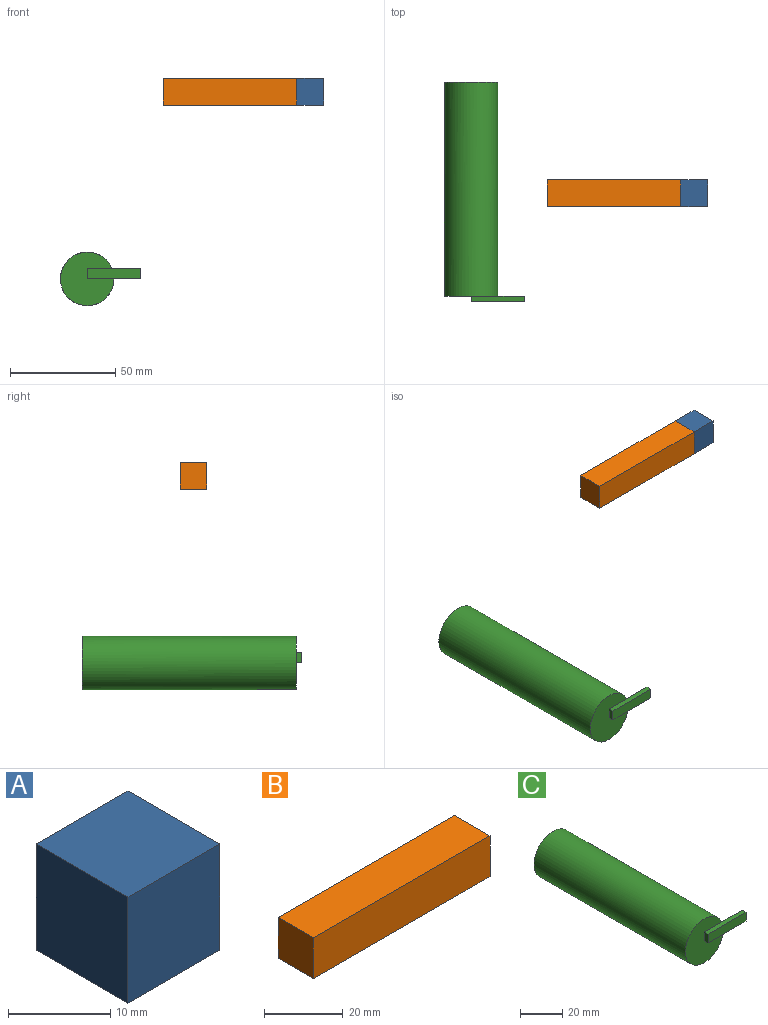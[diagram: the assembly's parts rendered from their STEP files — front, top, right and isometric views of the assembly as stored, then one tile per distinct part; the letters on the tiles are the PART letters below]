
ASSEMBLY  parts=3 mates=1
PART A: 6 faces, bbox 12.7x12.7x12.7 mm
  f0: plane 12.7x12.7mm, normal (0,0,-1), area 161.3mm2, adj f1,f3,f4,f5
  f1: plane 12.7x12.7mm, normal (1,0,0), area 161.3mm2, adj f0,f2,f4,f5
  f2: plane 12.7x12.7mm, normal (0,0,1), area 161.3mm2, adj f1,f3,f4,f5
  f3: plane 12.7x12.7mm, normal (-1,0,0), area 161.3mm2, adj f0,f2,f4,f5
  f4: plane 12.7x12.7mm, normal (0,-1,0), area 161.3mm2, adj f0,f1,f2,f3
  f5: plane 12.7x12.7mm, normal (0,1,0), area 161.3mm2, adj f0,f1,f2,f3
PART B: 6 faces, bbox 63.5x12.7x12.7 mm
  f0: plane 63.5x12.7mm, normal (0,0,-1), area 806.5mm2, adj f1,f3,f4,f5
  f1: plane 12.7x12.7mm, normal (1,0,0), area 161.3mm2, adj f0,f2,f4,f5
  f2: plane 63.5x12.7mm, normal (0,0,1), area 806.5mm2, adj f1,f3,f4,f5
  f3: plane 12.7x12.7mm, normal (-1,0,0), area 161.3mm2, adj f0,f2,f4,f5
  f4: plane 63.5x12.7mm, normal (0,-1,0), area 806.5mm2, adj f0,f1,f2,f3
  f5: plane 63.5x12.7mm, normal (0,1,0), area 806.5mm2, adj f0,f1,f2,f3
PART C: 9 faces, bbox 38.1x104.1x25.4 mm
  f0: plane 25.4x25.4mm, normal (0,-1,0), area 444mm2, adj f1,f4,f5,f6
  f1: cylinder r=12.7mm len=101.6mm, axis (0,1,0), area 8107.3mm2, adj f0,f2,f3
  f2: plane 25.4x25.4mm, normal (0,1,0), area 506.7mm2, adj f1
  f3: plane 13.76x5.08mm, normal (0,1,0), area 66.3mm2, adj f1,f4,f6,f7
  f4: plane 25.4x2.54mm, normal (0,0,1), area 64.5mm2, adj f0,f3,f5,f7,f8
  f5: plane 5.08x2.54mm, normal (-1,0,0), area 12.9mm2, adj f0,f4,f6,f8
  f6: plane 25.4x2.54mm, normal (0,0,-1), area 64.5mm2, adj f0,f3,f5,f7,f8
  f7: plane 5.08x2.54mm, normal (1,0,0), area 12.9mm2, adj f3,f4,f6,f8
  f8: plane 25.4x5.08mm, normal (0,-1,0), area 129mm2, adj f4,f5,f6,f7
PLACE A t=(108.4,-3.44,39.01)mm
PLACE B t=(73.61,-3.44,111.19)mm
PLACE C t=(2.55,43.02,-21.28)mm
MATE slider A.f3 <-> B.f1  axis (-1,0,0) through (102.05,-9.79,67.58)mm
